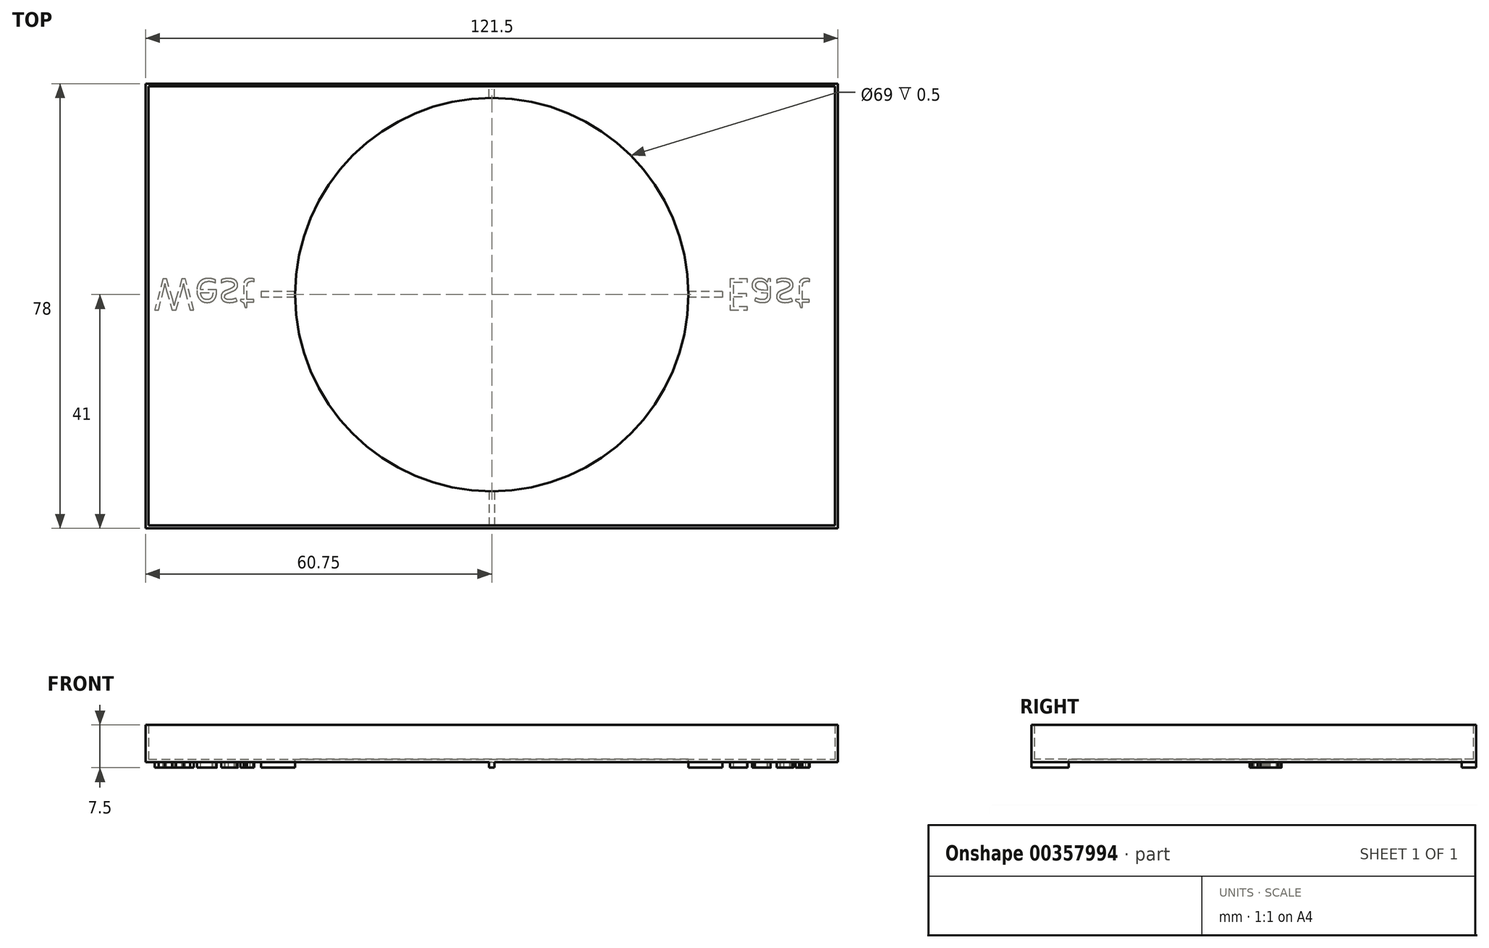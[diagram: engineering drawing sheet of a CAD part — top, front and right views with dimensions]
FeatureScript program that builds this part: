
annotation { "Feature Type Name" : "Feature", "Feature Type Description" : "" }
export const myFeature = defineFeature(function(context is Context, id is Id, definition is map)
    precondition{}
    {
        {
            var Q0;
            Q0=qCreatedBy(makeId("Top.planeOp"),FACE);
            var sketch = newSketch(context, id + "F0", { "sketchPlane" : qUnion([Q0])});
            skLineSegment(sketch, "E0.bottom", {"start": v(-60.75, 37) * mm, "end": v(60.75, 37) * mm});
            skLineSegment(sketch, "E0.top", {"start": v(-60.75, -41) * mm, "end": v(60.75, -41) * mm});
            skLineSegment(sketch, "E0.left", {"start": v(-60.75, 37) * mm, "end": v(-60.75, -41) * mm});
            skLineSegment(sketch, "E0.right", {"start": v(60.75, 37) * mm, "end": v(60.75, -41) * mm});
            skSolve(sketch);
        }
        {
            var Q0;
            Q0=makeQuery(id+"F0.imprint","IMPRINT",FACE,{"disambiguationData":[TD([[makeQuery(id+"F0.imprint","IMPRINT",EDGE,{"derivedFrom":sQuery(id+"F0.wireOp",EDGE,"E0.bottom")}),-1.0]])]});
            extrude(context, id + "F1", {"entities" : qUnion([Q0]), "depth" : 0.5 * mm});
        }
        {
            var Q0;
            Q0=makeQuery(id+"F1.opExtrude","CAP_FACE",FACE,{"disambiguationData":[OSD([sQuery(id+"F0.wireOp",EDGE,"E0.bottom"),sQuery(id+"F0.wireOp",EDGE,"E0.top"),sQuery(id+"F0.wireOp",EDGE,"E0.left"),sQuery(id+"F0.wireOp",EDGE,"E0.right")])],"isStart":false});
            var sketch = newSketch(context, id + "F2", { "sketchPlane" : qUnion([Q0])});
            skLineSegment(sketch, "E1.bottom", {"start": v(-60.25, 36.5) * mm, "end": v(60.25, 36.5) * mm});
            skLineSegment(sketch, "E1.top", {"start": v(-60.25, -40.5) * mm, "end": v(60.25, -40.5) * mm});
            skLineSegment(sketch, "E1.left", {"start": v(-60.25, 36.5) * mm, "end": v(-60.25, -40.5) * mm});
            skLineSegment(sketch, "E1.right", {"start": v(60.25, 36.5) * mm, "end": v(60.25, -40.5) * mm});
            skSolve(sketch);
        }
        {
            var Q0;
            Q0=makeQuery(id+"F2.imprint","IMPRINT",FACE,{"disambiguationData":[TD([[makeQuery(id+"F2.imprint","IMPRINT",EDGE,{"derivedFrom":sQuery(id+"F2.wireOp",EDGE,"E1.bottom")}),1.0]])]});
            extrude(context, id + "F3", {"entities" : qUnion([Q0]), "operationType" : NewBodyOperationType.ADD, "depth" : 6 * mm});
        }
        {
            var Q0;
            Q0=makeQuery(id+"F1.opExtrude","CAP_FACE",FACE,{"disambiguationData":[OSD([sQuery(id+"F0.wireOp",EDGE,"E0.bottom"),sQuery(id+"F0.wireOp",EDGE,"E0.top"),sQuery(id+"F0.wireOp",EDGE,"E0.left"),sQuery(id+"F0.wireOp",EDGE,"E0.right")])],"isStart":false});
            var sketch = newSketch(context, id + "F4", { "sketchPlane" : qUnion([Q0])});
            skCircle(sketch, "E2", {"center": v(0, 0) * mm, "radius": 34.5 * mm});
            skSolve(sketch);
        }
        {
            var Q0;
            Q0=makeQuery(id+"F4.imprint","IMPRINT",FACE,{"disambiguationData":[TD([[makeQuery(id+"F4.imprint","IMPRINT",EDGE,{"derivedFrom":sQuery(id+"F4.wireOp",EDGE,"E2")}),1.0]])]});
            extrude(context, id + "F5", {"entities" : qUnion([Q0]), "operationType" : NewBodyOperationType.REMOVE, "endBound" : BoundingType.THROUGH_ALL, "oppositeDirection" : true, "depth" : 25 * mm});
        }
        {
            var Q0;
            Q0=makeQuery(id+"F0.imprint","IMPRINT",FACE,{"disambiguationData":[TD([[makeQuery(id+"F0.imprint","IMPRINT",EDGE,{"derivedFrom":sQuery(id+"F0.wireOp",EDGE,"E0.bottom")}),-1.0]])]});
            var sketch = newSketch(context, id + "F6", { "sketchPlane" : qUnion([Q0])});
            skLineSegment(sketch, "E3.bottom", {"start": v(0.5, -34.5) * mm, "end": v(-0.5, -34.5) * mm});
            skLineSegment(sketch, "E3.top", {"start": v(0.5, -41) * mm, "end": v(-0.5, -41) * mm});
            skLineSegment(sketch, "E3.left", {"start": v(0.5, -34.5) * mm, "end": v(0.5, -41) * mm});
            skLineSegment(sketch, "E3.right", {"start": v(-0.5, -34.5) * mm, "end": v(-0.5, -41) * mm});
            skPoint(sketch, "E3.middle", {"position": v(0, -37.75) * mm});
            skSolve(sketch);
        }
        {
            var Q0;
            Q0 = qSketchRegion(id + "F6", true);
            extrude(context, id + "F7", {"entities" : qUnion([Q0]), "operationType" : NewBodyOperationType.ADD, "oppositeDirection" : true, "depth" : 1 * mm});
        }
        {
            var Q0;
            Q0=makeQuery(id+"F0.imprint","IMPRINT",FACE,{"disambiguationData":[TD([[makeQuery(id+"F0.imprint","IMPRINT",EDGE,{"derivedFrom":sQuery(id+"F0.wireOp",EDGE,"E0.bottom")}),-1.0]])]});
            var sketch = newSketch(context, id + "F8", { "sketchPlane" : qUnion([Q0])});
            skLineSegment(sketch, "E4.bottom", {"start": v(-0.5, 34.5) * mm, "end": v(0.5, 34.5) * mm});
            skLineSegment(sketch, "E4.top", {"start": v(-0.5, 37) * mm, "end": v(0.5, 37) * mm});
            skLineSegment(sketch, "E4.left", {"start": v(-0.5, 34.5) * mm, "end": v(-0.5, 37) * mm});
            skLineSegment(sketch, "E4.right", {"start": v(0.5, 34.5) * mm, "end": v(0.5, 37) * mm});
            skPoint(sketch, "E4.middle", {"position": v(0, 35.75) * mm});
            skSolve(sketch);
        }
        {
            var Q0;
            Q0 = qSketchRegion(id + "F8", true);
            extrude(context, id + "F9", {"entities" : qUnion([Q0]), "operationType" : NewBodyOperationType.ADD, "oppositeDirection" : true, "depth" : 1 * mm});
        }
        {
            var Q0;
            Q0=makeQuery(id+"F0.imprint","IMPRINT",FACE,{"disambiguationData":[TD([[makeQuery(id+"F0.imprint","IMPRINT",EDGE,{"derivedFrom":sQuery(id+"F0.wireOp",EDGE,"E0.bottom")}),-1.0]])]});
            var sketch = newSketch(context, id + "F10", { "sketchPlane" : qUnion([Q0])});
            skLineSegment(sketch, "E5.bottom", {"start": v(40.5, 0.5) * mm, "end": v(34.5, 0.5) * mm});
            skLineSegment(sketch, "E5.top", {"start": v(40.5, -0.5) * mm, "end": v(34.5, -0.5) * mm});
            skLineSegment(sketch, "E5.left", {"start": v(40.5, 0.5) * mm, "end": v(40.5, -0.5) * mm});
            skLineSegment(sketch, "E5.right", {"start": v(34.5, 0.5) * mm, "end": v(34.5, -0.5) * mm});
            skPoint(sketch, "E5.middle", {"position": v(37.5, 0) * mm});
            skSolve(sketch);
        }
        {
            var Q0;
            Q0 = qSketchRegion(id + "F10", true);
            extrude(context, id + "F11", {"entities" : qUnion([Q0]), "operationType" : NewBodyOperationType.ADD, "oppositeDirection" : true, "depth" : 1 * mm});
        }
        {
            var Q0;
            Q0=makeQuery(id+"F0.imprint","IMPRINT",FACE,{"disambiguationData":[TD([[makeQuery(id+"F0.imprint","IMPRINT",EDGE,{"derivedFrom":sQuery(id+"F0.wireOp",EDGE,"E0.bottom")}),-1.0]])]});
            var sketch = newSketch(context, id + "F12", { "sketchPlane" : qUnion([Q0])});
            skLineSegment(sketch, "E6.bottom", {"start": v(-34.5, 0.5) * mm, "end": v(-40.5, 0.5) * mm});
            skLineSegment(sketch, "E6.top", {"start": v(-34.5, -0.5) * mm, "end": v(-40.5, -0.5) * mm});
            skLineSegment(sketch, "E6.left", {"start": v(-34.5, 0.5) * mm, "end": v(-34.5, -0.5) * mm});
            skLineSegment(sketch, "E6.right", {"start": v(-40.5, 0.5) * mm, "end": v(-40.5, -0.5) * mm});
            skPoint(sketch, "E6.middle", {"position": v(-37.5, 0) * mm});
            skSolve(sketch);
        }
        {
            var Q0;
            Q0 = qSketchRegion(id + "F12", true);
            extrude(context, id + "F13", {"entities" : qUnion([Q0]), "operationType" : NewBodyOperationType.ADD, "oppositeDirection" : true, "depth" : 1 * mm});
        }
        {
            var Q0;
            Q0=qCreatedBy(makeId("Top.planeOp"),FACE);
            var sketch = newSketch(context, id + "F14", { "sketchPlane" : qUnion([Q0])});
            skLineSegment(sketch, "E7", {"start": v(0, -121.77) * mm, "end": v(0, 133.6) * mm});
            skSolve(sketch);
        }
        {
            var Q0;
            Q0=sQuery(id+"F14.wireOp",EDGE,"E7");
            cPlane(context, id + "F15", {"entities" : qUnion([Q0]), "cplaneType" : CPlaneType.LINE_ANGLE, "offset" : 25 * mm, "angle" : 180 * degree, "width" : 150 * mm, "height" : 150 * mm});
        }
        {
            var Q0;
            Q0=qCreatedBy(id+"F15.planeOp",FACE);
            var sketch = newSketch(context, id + "F16", { "sketchPlane" : qUnion([Q0])});
            skText(sketch, "E8", { "text": "West", "fontName": "OpenSans-Regular.ttf"});
            skText(sketch, "E9", { "text": "East", "fontName": "OpenSans-Regular.ttf"});
            const initialGuessF16  = {"E8": [-0.05925, -0.00275, 1, 0, 0.0055], "E9": [0.04108, -0.00275, 1, 0, 0.0055]};
            skSetInitialGuess(sketch, initialGuessF16);
            skSolve(sketch);
        }
        {
            var Q0;
            Q0 = qSketchRegion(id + "F16", true);
            extrude(context, id + "F17", {"entities" : qUnion([Q0]), "operationType" : NewBodyOperationType.ADD, "depth" : 1 * mm});
        }
    });
